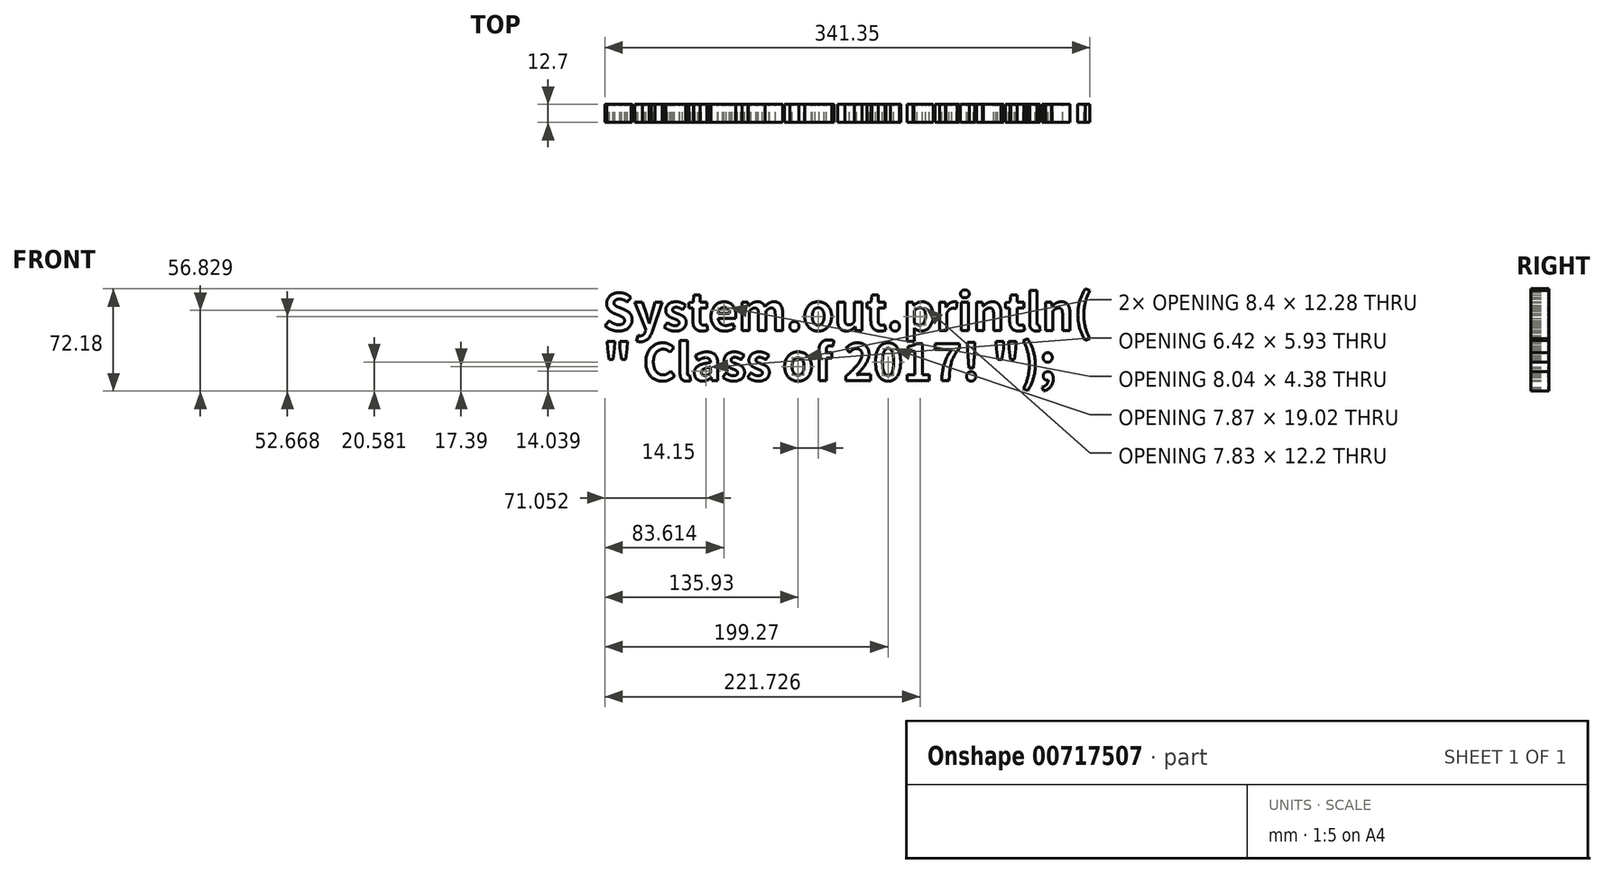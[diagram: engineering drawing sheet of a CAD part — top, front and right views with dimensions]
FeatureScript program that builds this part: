
annotation { "Feature Type Name" : "Feature", "Feature Type Description" : "" }
export const myFeature = defineFeature(function(context is Context, id is Id, definition is map)
    precondition{}
    {
        {
            var Q0;
            Q0=qCreatedBy(makeId("Front.planeOp"),FACE);
            var sketch = newSketch(context, id + "F0", { "sketchPlane" : qUnion([Q0])});
            skText(sketch, "E0", { "text": "System.out.println(\n\" Class of 2017! \");", "fontName": "NotoSansCJKjp-Bold.otf"});
            const initialGuessF0  = {"E0": [-0.00341, -0.02993, 1, 0, 0.0254]};
            skSetInitialGuess(sketch, initialGuessF0);
            skSolve(sketch);
        }
        {
            var Q0;
            Q0 = qSketchRegion(id + "F0", true);
            extrude(context, id + "F1", {"entities" : qUnion([Q0]), "depth" : 12.7 * mm, "offsetDistance" : 25.4 * mm});
        }
    });
